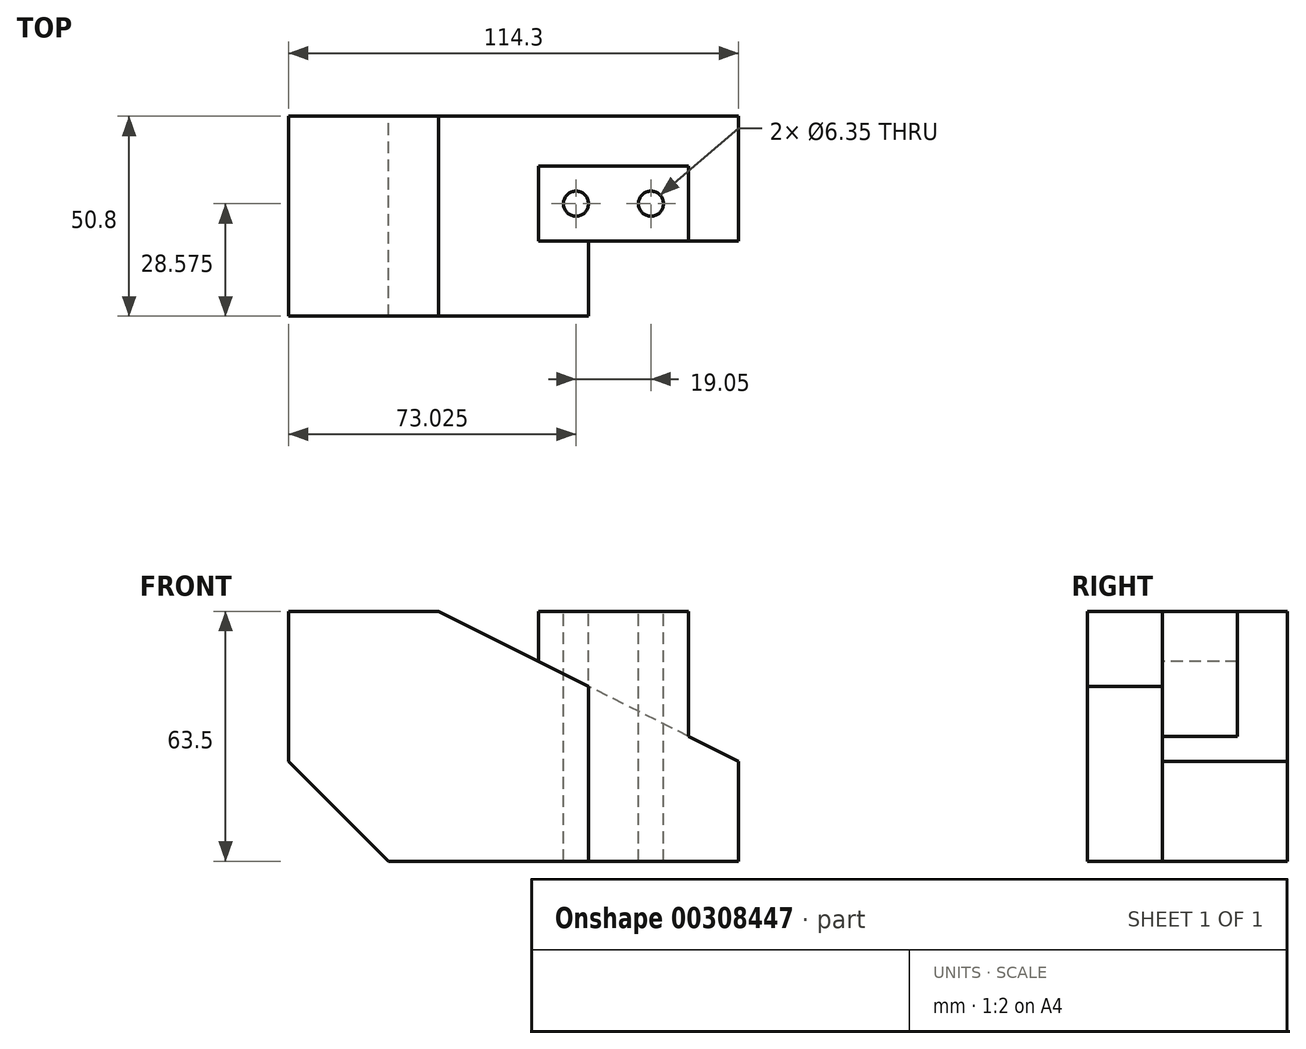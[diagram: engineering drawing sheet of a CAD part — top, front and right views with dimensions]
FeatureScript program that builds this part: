
annotation { "Feature Type Name" : "Feature", "Feature Type Description" : "" }
export const myFeature = defineFeature(function(context is Context, id is Id, definition is map)
    precondition{}
    {
        {
            var Q0;
            Q0=qCreatedBy(makeId("Front.planeOp"),FACE);
            var sketch = newSketch(context, id + "F0", { "sketchPlane" : qUnion([Q0])});
            skLineSegment(sketch, "E0", {"start": v(25.4, 0) * mm, "end": v(114.3, 0) * mm});
            skLineSegment(sketch, "E1", {"start": v(114.3, 0) * mm, "end": v(114.3, 25.4) * mm});
            skLineSegment(sketch, "E2", {"start": v(114.3, 25.4) * mm, "end": v(38.1, 63.5) * mm});
            skLineSegment(sketch, "E3", {"start": v(38.1, 63.5) * mm, "end": v(0, 63.5) * mm});
            skLineSegment(sketch, "E4", {"start": v(0, 63.5) * mm, "end": v(0, 25.4) * mm});
            skLineSegment(sketch, "E5", {"start": v(101.6, 0) * mm, "end": v(101.6, 63.5) * mm});
            skLineSegment(sketch, "E6", {"start": v(101.6, 63.5) * mm, "end": v(63.5, 63.5) * mm});
            skLineSegment(sketch, "E7", {"start": v(63.5, 63.5) * mm, "end": v(63.5, 0) * mm});
            skLineSegment(sketch, "E8", {"start": v(0, 25.4) * mm, "end": v(25.4, 0) * mm});
            skPoint(sketch, "E9.orphan", {"position": v(0, 0) * mm});
            skLineSegment(sketch, "E10", {"start": v(76.2, 0) * mm, "end": v(76.2, 44.45) * mm});
            skSolve(sketch);
        }
        {
            var Q0;
            {var subQ0=sQuery(id+"F0.wireOp",EDGE,"E3");Q0=makeQuery(id+"F0.imprint","IMPRINT",FACE,{"disambiguationData":[TD([[makeQuery(id+"F0.imprint","IMPRINT",EDGE,{"derivedFrom":subQ0}),1.0]])]});}
            var Q1;
            {var subQ3=sQuery(id+"F0.wireOp",EDGE,"E10");Q1=makeQuery(id+"F0.imprint","IMPRINT",FACE,{"disambiguationData":[TD([[makeQuery(id+"F0.imprint","IMPRINT",EDGE,{"derivedFrom":subQ3}),1.0]])]});}
            extrude(context, id + "F1", {"entities" : qUnion([Q0, Q1]), "depth" : 50.8 * mm});
        }
        {
            var Q0;
            {var subQ3=sQuery(id+"F0.wireOp",EDGE,"E10");Q0=makeQuery(id+"F0.imprint","IMPRINT",FACE,{"disambiguationData":[TD([[makeQuery(id+"F0.imprint","IMPRINT",EDGE,{"derivedFrom":subQ3}),-1.0]])]});}
            var Q1;
            {var subQ0=sQuery(id+"F0.wireOp",EDGE,"E1");Q1=makeQuery(id+"F0.imprint","IMPRINT",FACE,{"disambiguationData":[TD([[makeQuery(id+"F0.imprint","IMPRINT",EDGE,{"derivedFrom":subQ0}),1.0]])]});}
            extrude(context, id + "F2", {"entities" : qUnion([Q0, Q1]), "operationType" : NewBodyOperationType.ADD, "depth" : 31.75 * mm});
        }
        {
            var Q0;
            Q0=makeQuery(id+"F2.opExtrude","CAP_FACE",FACE,{"disambiguationData":[OSD([sQuery(id+"F0.wireOp",EDGE,"E0"),sQuery(id+"F0.wireOp",EDGE,"E1"),sQuery(id+"F0.wireOp",EDGE,"E2"),sQuery(id+"F0.wireOp",EDGE,"E10")])],"isStart":false});
            var sketch = newSketch(context, id + "F3", { "sketchPlane" : qUnion([Q0])});
            skLineSegment(sketch, "E11.0", {"start": v(101.6, 63.5) * mm, "end": v(63.5, 63.5) * mm});
            skLineSegment(sketch, "E12.0", {"start": v(101.6, 0) * mm, "end": v(101.6, 63.5) * mm});
            skLineSegment(sketch, "E13.0", {"start": v(63.5, 63.5) * mm, "end": v(63.5, 0) * mm});
            skLineSegment(sketch, "E14.0", {"start": v(114.3, 25.4) * mm, "end": v(38.1, 63.5) * mm});
            skSolve(sketch);
        }
        {
            var Q0;
            {var subQ1=sQuery(id+"F3.wireOp",EDGE,"E11.0");Q0=makeQuery(id+"F3.imprint","IMPRINT",FACE,{"disambiguationData":[TD([[makeQuery(id+"F3.imprint","IMPRINT",EDGE,{"derivedFrom":subQ1}),1.0]])]});}
            extrude(context, id + "F4", {"entities" : qUnion([Q0]), "operationType" : NewBodyOperationType.ADD, "oppositeDirection" : true, "depth" : 19.05 * mm});
        }
        {
            var Q0;
            Q0=makeQuery(id+"F4.opExtrude","SWEPT_FACE",FACE,{"disambiguationData":[OSD([sQuery(id+"F3.wireOp",EDGE,"E11.0")])]});
            var sketch = newSketch(context, id + "F5", { "sketchPlane" : qUnion([Q0])});
            skLineSegment(sketch, "E15", {"start": v(63.5, -22.22) * mm, "end": v(101.6, -22.22) * mm, "construction": true});
            skCircle(sketch, "E16", {"center": v(73.03, -22.22) * mm, "radius": 3.18 * mm});
            skCircle(sketch, "E17", {"center": v(92.08, -22.22) * mm, "radius": 3.18 * mm});
            skSolve(sketch);
        }
        {
            var Q0;
            Q0 = qSketchRegion(id + "F5", true);
            extrude(context, id + "F6", {"entities" : qUnion([Q0]), "operationType" : NewBodyOperationType.REMOVE, "endBound" : BoundingType.THROUGH_ALL, "oppositeDirection" : true, "depth" : 25.4 * mm});
        }
    });
